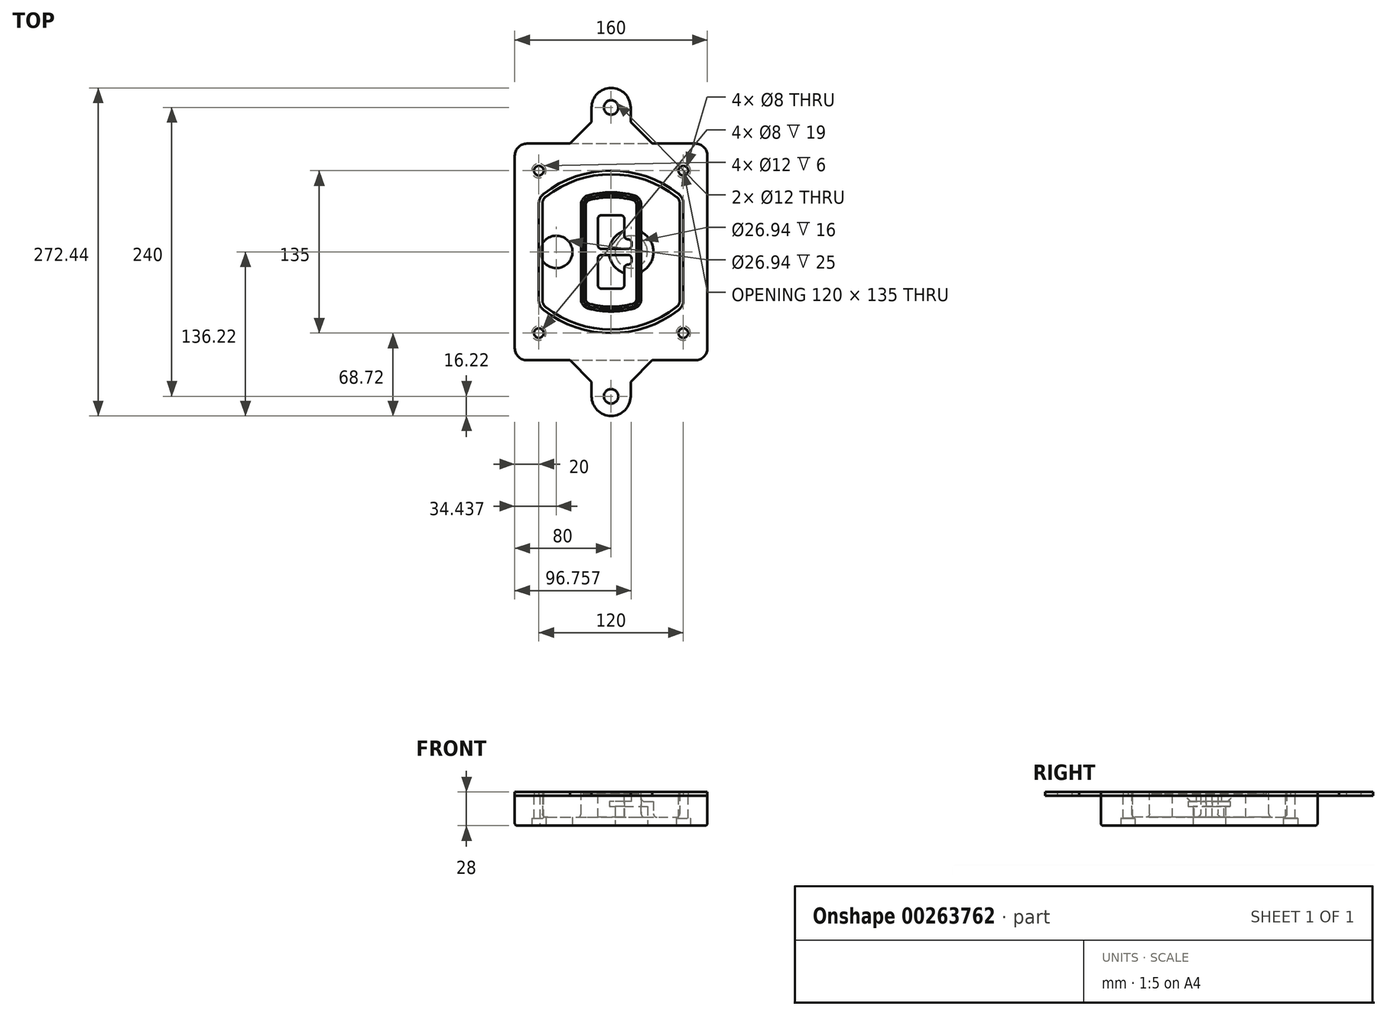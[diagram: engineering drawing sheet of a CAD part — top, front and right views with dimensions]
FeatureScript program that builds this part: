
annotation { "Feature Type Name" : "Feature", "Feature Type Description" : "" }
export const myFeature = defineFeature(function(context is Context, id is Id, definition is map)
    precondition{}
    {
        {
            var Q0;
            Q0=qCreatedBy(makeId("Top.planeOp"),FACE);
            var sketch = newSketch(context, id + "F0", { "sketchPlane" : qUnion([Q0])});
            skPoint(sketch, "E0.rect.middle", {"position": v(0, 0) * mm});
            skLineSegment(sketch, "E1.bottom", {"start": v(-70, -90) * mm, "end": v(70, -90) * mm});
            skLineSegment(sketch, "E1.top", {"start": v(-70, 90) * mm, "end": v(70, 90) * mm});
            skLineSegment(sketch, "E1.left", {"start": v(-80, -80) * mm, "end": v(-80, 80) * mm});
            skLineSegment(sketch, "E1.right", {"start": v(80, -80) * mm, "end": v(80, 80) * mm});
            skLineSegment(sketch, "E2", {"start": v(-80, 90) * mm, "end": v(80, -90) * mm, "construction": true});
            skLineSegment(sketch, "E3", {"start": v(80, 90) * mm, "end": v(-80, -90) * mm, "construction": true});
            skCircle(sketch, "E4", {"center": v(-60, 67.5) * mm, "radius": 4 * mm});
            skCircle(sketch, "E5", {"center": v(60, 67.5) * mm, "radius": 4 * mm});
            skCircle(sketch, "E6", {"center": v(60, -67.5) * mm, "radius": 4 * mm});
            skCircle(sketch, "E7", {"center": v(-60, -67.5) * mm, "radius": 4 * mm});
            skLineSegment(sketch, "E8", {"start": v(-60, 67.5) * mm, "end": v(60, 67.5) * mm, "construction": true});
            skLineSegment(sketch, "E9", {"start": v(60, 67.5) * mm, "end": v(60, -67.5) * mm, "construction": true});
            skLineSegment(sketch, "E10", {"start": v(60, -67.5) * mm, "end": v(-60, -67.5) * mm, "construction": true});
            skLineSegment(sketch, "E11", {"start": v(-60, -67.5) * mm, "end": v(-60, 67.5) * mm, "construction": true});
            skLineSegment(sketch, "E12", {"start": v(-60, 40.3) * mm, "end": v(-60, -40.3) * mm});
            skLineSegment(sketch, "E13", {"start": v(60, 40.3) * mm, "end": v(60, -40.3) * mm});
            skArc(sketch, "E14", {"start": v(56.15, 48.18) * mm, "mid": v(0, 67.5) * mm, "end": v(-56.15, 48.18) * mm});
            skArc(sketch, "E15", {"start": v(-56.15, -48.18) * mm, "mid": v(0, -67.5) * mm, "end": v(56.15, -48.18) * mm});
            skLineSegment(sketch, "E16", {"start": v(-60, 0) * mm, "end": v(60, 0) * mm, "construction": true});
            skPoint(sketch, "E17.visualSharp", {"position": v(-60, -45) * mm});
            skArc(sketch, "E17.filletArc", {"start": v(-60, -40.3) * mm, "mid": v(-58.99, -44.68) * mm, "end": v(-56.15, -48.18) * mm});
            skPoint(sketch, "E18.visualSharp", {"position": v(-60, 45) * mm});
            skArc(sketch, "E18.filletArc", {"start": v(-56.15, 48.18) * mm, "mid": v(-58.99, 44.68) * mm, "end": v(-60, 40.3) * mm});
            skPoint(sketch, "E19.visualSharp", {"position": v(60, 45) * mm});
            skArc(sketch, "E19.filletArc", {"start": v(60, 40.3) * mm, "mid": v(58.99, 44.68) * mm, "end": v(56.15, 48.18) * mm});
            skPoint(sketch, "E20.visualSharp", {"position": v(60, -45) * mm});
            skArc(sketch, "E20.filletArc", {"start": v(56.15, -48.18) * mm, "mid": v(58.99, -44.68) * mm, "end": v(60, -40.3) * mm});
            skPoint(sketch, "E21.visualSharp", {"position": v(-80, 90) * mm});
            skArc(sketch, "E21.filletArc", {"start": v(-70, 90) * mm, "mid": v(-77.07, 87.07) * mm, "end": v(-80, 80) * mm});
            skPoint(sketch, "E22.visualSharp", {"position": v(80, 90) * mm});
            skArc(sketch, "E22.filletArc", {"start": v(80, 80) * mm, "mid": v(77.07, 87.07) * mm, "end": v(70, 90) * mm});
            skPoint(sketch, "E23.visualSharp", {"position": v(80, -90) * mm});
            skArc(sketch, "E23.filletArc", {"start": v(70, -90) * mm, "mid": v(77.07, -87.07) * mm, "end": v(80, -80) * mm});
            skPoint(sketch, "E24.visualSharp", {"position": v(-80, -90) * mm});
            skArc(sketch, "E24.filletArc", {"start": v(-80, -80) * mm, "mid": v(-77.07, -87.07) * mm, "end": v(-70, -90) * mm});
            skArc(sketch, "E25.0", {"start": v(57, 40.3) * mm, "mid": v(56.3, 43.36) * mm, "end": v(54.3, 45.81) * mm});
            skLineSegment(sketch, "E25.1", {"start": v(57, 40.3) * mm, "end": v(57, -40.3) * mm});
            skArc(sketch, "E25.2", {"start": v(54.3, -45.81) * mm, "mid": v(56.3, -43.36) * mm, "end": v(57, -40.3) * mm});
            skArc(sketch, "E25.3", {"start": v(-54.3, -45.81) * mm, "mid": v(0, -64.5) * mm, "end": v(54.3, -45.81) * mm});
            skArc(sketch, "E25.4", {"start": v(-57, -40.3) * mm, "mid": v(-56.3, -43.36) * mm, "end": v(-54.3, -45.81) * mm});
            skArc(sketch, "E25.5", {"start": v(54.3, 45.81) * mm, "mid": v(0, 64.5) * mm, "end": v(-54.3, 45.81) * mm});
            skLineSegment(sketch, "E25.6", {"start": v(-57, 40.3) * mm, "end": v(-57, -40.3) * mm});
            skArc(sketch, "E25.7", {"start": v(-54.3, 45.81) * mm, "mid": v(-56.3, 43.36) * mm, "end": v(-57, 40.3) * mm});
            skArc(sketch, "E26.0", {"start": v(-58.62, 51.33) * mm, "mid": v(-62.58, 46.43) * mm, "end": v(-64, 40.3) * mm});
            skArc(sketch, "E26.1", {"start": v(58.62, 51.33) * mm, "mid": v(0, 71.5) * mm, "end": v(-58.62, 51.33) * mm});
            skArc(sketch, "E26.2", {"start": v(64, 40.3) * mm, "mid": v(62.58, 46.43) * mm, "end": v(58.62, 51.33) * mm});
            skLineSegment(sketch, "E26.3", {"start": v(64, 40.3) * mm, "end": v(64, -40.3) * mm});
            skArc(sketch, "E26.4", {"start": v(58.62, -51.33) * mm, "mid": v(62.58, -46.43) * mm, "end": v(64, -40.3) * mm});
            skLineSegment(sketch, "E26.5", {"start": v(-64, 40.3) * mm, "end": v(-64, -40.3) * mm});
            skArc(sketch, "E26.6", {"start": v(-58.62, -51.33) * mm, "mid": v(0, -71.5) * mm, "end": v(58.62, -51.33) * mm});
            skArc(sketch, "E26.7", {"start": v(-64, -40.3) * mm, "mid": v(-62.58, -46.43) * mm, "end": v(-58.62, -51.33) * mm});
            skSolve(sketch);
        }
        {
            var Q0;
            Q0=makeQuery(id+"F0.imprint","IMPRINT",FACE,{"disambiguationData":[TD([[makeQuery(id+"F0.imprint","IMPRINT",EDGE,{"derivedFrom":sQuery(id+"F0.wireOp",EDGE,"E1.bottom")}),1.0]])]});
            var Q1;
            Q1=makeQuery(id+"F0.imprint","IMPRINT",FACE,{"disambiguationData":[TD([[makeQuery(id+"F0.imprint","IMPRINT",EDGE,{"derivedFrom":sQuery(id+"F0.wireOp",EDGE,"E12")}),1.0]])]});
            var Q2;
            Q2=makeQuery(id+"F0.imprint","IMPRINT",FACE,{"disambiguationData":[TD([[makeQuery(id+"F0.imprint","IMPRINT",EDGE,{"derivedFrom":sQuery(id+"F0.wireOp",EDGE,"E25.0")}),1.0]])]});
            var Q3;
            Q3=makeQuery(id+"F0.imprint","IMPRINT",FACE,{"disambiguationData":[TD([[makeQuery(id+"F0.imprint","IMPRINT",EDGE,{"derivedFrom":sQuery(id+"F0.wireOp",EDGE,"E12")}),-1.0]])]});
            extrude(context, id + "F1", {"entities" : qUnion([Q0, Q1, Q2, Q3]), "oppositeDirection" : true, "depth" : 25 * mm});
        }
        {
            var Q0;
            Q0=makeQuery(id+"F0.imprint","IMPRINT",FACE,{"disambiguationData":[TD([[makeQuery(id+"F0.imprint","IMPRINT",EDGE,{"derivedFrom":sQuery(id+"F0.wireOp",EDGE,"E12")}),1.0]])]});
            extrude(context, id + "F2", {"entities" : qUnion([Q0]), "operationType" : NewBodyOperationType.ADD, "depth" : 3 * mm});
        }
        {
            var Q0;
            Q0=makeQuery(id+"F0.imprint","IMPRINT",FACE,{"disambiguationData":[TD([[makeQuery(id+"F0.imprint","IMPRINT",EDGE,{"derivedFrom":sQuery(id+"F0.wireOp",EDGE,"E25.0")}),1.0]])]});
            extrude(context, id + "F3", {"entities" : qUnion([Q0]), "operationType" : NewBodyOperationType.REMOVE, "oppositeDirection" : true, "depth" : 18 * mm});
        }
        {
            var Q0;
            Q0=makeQuery(id+"F2.opExtrude","CAP_FACE",FACE,{"disambiguationData":[OSD([sQuery(id+"F0.wireOp",EDGE,"E12"),sQuery(id+"F0.wireOp",EDGE,"E13"),sQuery(id+"F0.wireOp",EDGE,"E14"),sQuery(id+"F0.wireOp",EDGE,"E15"),sQuery(id+"F0.wireOp",EDGE,"E17.filletArc"),sQuery(id+"F0.wireOp",EDGE,"E18.filletArc"),sQuery(id+"F0.wireOp",EDGE,"E19.filletArc"),sQuery(id+"F0.wireOp",EDGE,"E20.filletArc"),sQuery(id+"F0.wireOp",EDGE,"E25.0"),sQuery(id+"F0.wireOp",EDGE,"E25.1"),sQuery(id+"F0.wireOp",EDGE,"E25.2"),sQuery(id+"F0.wireOp",EDGE,"E25.3"),sQuery(id+"F0.wireOp",EDGE,"E25.4"),sQuery(id+"F0.wireOp",EDGE,"E25.5"),sQuery(id+"F0.wireOp",EDGE,"E25.6"),sQuery(id+"F0.wireOp",EDGE,"E25.7")])],"isStart":false});
            var sketch = newSketch(context, id + "F4", { "sketchPlane" : qUnion([Q0])});
            skArc(sketch, "E27.0", {"start": v(-19.08, -46.97) * mm, "mid": v(0, -49.5) * mm, "end": v(19.08, -46.97) * mm});
            skArc(sketch, "E28.0", {"start": v(19.08, 46.97) * mm, "mid": v(0, 49.5) * mm, "end": v(-19.08, 46.97) * mm});
            skLineSegment(sketch, "E29", {"start": v(-25, 39.25) * mm, "end": v(-25, -39.25) * mm});
            skLineSegment(sketch, "E30", {"start": v(25, 39.25) * mm, "end": v(25, -39.25) * mm});
            skLineSegment(sketch, "E31", {"start": v(-25, 45.1) * mm, "end": v(25, 45.1) * mm, "construction": true});
            skLineSegment(sketch, "E32", {"start": v(-25, -45.1) * mm, "end": v(25, -45.1) * mm, "construction": true});
            skPoint(sketch, "E33.visualSharp", {"position": v(-25, 45.1) * mm});
            skArc(sketch, "E33.filletArc", {"start": v(-19.08, 46.97) * mm, "mid": v(-23.35, 44.11) * mm, "end": v(-25, 39.25) * mm});
            skPoint(sketch, "E34.visualSharp", {"position": v(25, 45.1) * mm});
            skArc(sketch, "E34.filletArc", {"start": v(25, 39.25) * mm, "mid": v(23.35, 44.11) * mm, "end": v(19.08, 46.97) * mm});
            skPoint(sketch, "E35.visualSharp", {"position": v(25, -45.1) * mm});
            skArc(sketch, "E35.filletArc", {"start": v(19.08, -46.97) * mm, "mid": v(23.35, -44.11) * mm, "end": v(25, -39.25) * mm});
            skPoint(sketch, "E36.visualSharp", {"position": v(-25, -45.1) * mm});
            skArc(sketch, "E36.filletArc", {"start": v(-25, -39.25) * mm, "mid": v(-23.35, -44.11) * mm, "end": v(-19.08, -46.97) * mm});
            skArc(sketch, "E37.0", {"start": v(54.3, 45.81) * mm, "mid": v(0, 64.5) * mm, "end": v(-54.3, 45.81) * mm});
            skArc(sketch, "E37.1", {"start": v(-54.3, 45.81) * mm, "mid": v(-56.3, 43.36) * mm, "end": v(-57, 40.3) * mm});
            skLineSegment(sketch, "E37.2", {"start": v(-57, 40.3) * mm, "end": v(-57, -40.3) * mm});
            skArc(sketch, "E37.3", {"start": v(-57, -40.3) * mm, "mid": v(-56.3, -43.36) * mm, "end": v(-54.3, -45.81) * mm});
            skArc(sketch, "E37.4", {"start": v(-54.3, -45.81) * mm, "mid": v(0, -64.5) * mm, "end": v(54.3, -45.81) * mm});
            skArc(sketch, "E37.5", {"start": v(54.3, -45.81) * mm, "mid": v(56.3, -43.36) * mm, "end": v(57, -40.3) * mm});
            skLineSegment(sketch, "E37.6", {"start": v(57, 40.3) * mm, "end": v(57, -40.3) * mm});
            skArc(sketch, "E37.7", {"start": v(57, 40.3) * mm, "mid": v(56.3, 43.36) * mm, "end": v(54.3, 45.81) * mm});
            skLineSegment(sketch, "E38.0", {"start": v(23, 39.25) * mm, "end": v(23, -39.25) * mm});
            skArc(sketch, "E38.1", {"start": v(18.56, -45.04) * mm, "mid": v(21.76, -42.9) * mm, "end": v(23, -39.25) * mm});
            skArc(sketch, "E38.2", {"start": v(-18.56, -45.04) * mm, "mid": v(0, -47.5) * mm, "end": v(18.56, -45.04) * mm});
            skArc(sketch, "E38.3", {"start": v(-23, -39.25) * mm, "mid": v(-21.76, -42.9) * mm, "end": v(-18.56, -45.04) * mm});
            skLineSegment(sketch, "E38.4", {"start": v(-23, 39.25) * mm, "end": v(-23, -39.25) * mm});
            skArc(sketch, "E38.5", {"start": v(23, 39.25) * mm, "mid": v(21.76, 42.9) * mm, "end": v(18.56, 45.04) * mm});
            skArc(sketch, "E38.6", {"start": v(-18.56, 45.04) * mm, "mid": v(-21.76, 42.9) * mm, "end": v(-23, 39.25) * mm});
            skArc(sketch, "E38.7", {"start": v(18.56, 45.04) * mm, "mid": v(0, 47.5) * mm, "end": v(-18.56, 45.04) * mm});
            skArc(sketch, "E39.0", {"start": v(21, 39.25) * mm, "mid": v(20.18, 41.68) * mm, "end": v(18.04, 43.1) * mm});
            skLineSegment(sketch, "E39.1", {"start": v(21, 39.25) * mm, "end": v(21, -39.25) * mm});
            skArc(sketch, "E39.2", {"start": v(18.04, -43.1) * mm, "mid": v(20.18, -41.68) * mm, "end": v(21, -39.25) * mm});
            skArc(sketch, "E39.3", {"start": v(-18.04, -43.1) * mm, "mid": v(0, -45.5) * mm, "end": v(18.04, -43.1) * mm});
            skArc(sketch, "E39.4", {"start": v(-21, -39.25) * mm, "mid": v(-20.18, -41.68) * mm, "end": v(-18.04, -43.1) * mm});
            skArc(sketch, "E39.5", {"start": v(18.04, 43.1) * mm, "mid": v(0, 45.5) * mm, "end": v(-18.04, 43.1) * mm});
            skLineSegment(sketch, "E39.6", {"start": v(-21, 39.25) * mm, "end": v(-21, -39.25) * mm});
            skArc(sketch, "E39.7", {"start": v(-18.04, 43.1) * mm, "mid": v(-20.18, 41.68) * mm, "end": v(-21, 39.25) * mm});
            skLineSegment(sketch, "E40", {"start": v(-25, 0) * mm, "end": v(25, 0) * mm, "construction": true});
            skLineSegment(sketch, "E41", {"start": v(-11, 5.5) * mm, "end": v(-11, 27.5) * mm});
            skLineSegment(sketch, "E42", {"start": v(-8, 30.5) * mm, "end": v(8, 30.5) * mm});
            skLineSegment(sketch, "E43", {"start": v(11, 27.5) * mm, "end": v(11, 13.5) * mm});
            skLineSegment(sketch, "E44", {"start": v(14, 10.5) * mm, "end": v(14, 10.5) * mm});
            skLineSegment(sketch, "E45", {"start": v(17, 7.5) * mm, "end": v(17, 5.5) * mm});
            skLineSegment(sketch, "E46", {"start": v(14, 2.5) * mm, "end": v(-8, 2.5) * mm});
            skPoint(sketch, "E47.visualSharp", {"position": v(-11, 30.5) * mm});
            skArc(sketch, "E47.filletArc", {"start": v(-8, 30.5) * mm, "mid": v(-10.12, 29.62) * mm, "end": v(-11, 27.5) * mm});
            skPoint(sketch, "E48.visualSharp", {"position": v(11, 30.5) * mm});
            skArc(sketch, "E48.filletArc", {"start": v(11, 27.5) * mm, "mid": v(10.12, 29.62) * mm, "end": v(8, 30.5) * mm});
            skPoint(sketch, "E49.visualSharp", {"position": v(11, 10.5) * mm});
            skArc(sketch, "E49.filletArc", {"start": v(11, 13.5) * mm, "mid": v(11.88, 11.38) * mm, "end": v(14, 10.5) * mm});
            skPoint(sketch, "E50.visualSharp", {"position": v(17, 10.5) * mm});
            skArc(sketch, "E50.filletArc", {"start": v(17, 7.5) * mm, "mid": v(16.12, 9.62) * mm, "end": v(14, 10.5) * mm});
            skPoint(sketch, "E51.visualSharp", {"position": v(17, 2.5) * mm});
            skArc(sketch, "E51.filletArc", {"start": v(14, 2.5) * mm, "mid": v(16.12, 3.38) * mm, "end": v(17, 5.5) * mm});
            skPoint(sketch, "E52.visualSharp", {"position": v(-11, 2.5) * mm});
            skArc(sketch, "E52.filletArc", {"start": v(-11, 5.5) * mm, "mid": v(-10.12, 3.38) * mm, "end": v(-8, 2.5) * mm});
            skLineSegment(sketch, "E53.0.MirrorCS", {"start": v(14, -2.5) * mm, "end": v(-8, -2.5) * mm});
            skArc(sketch, "E54.0.MirrorCS", {"start": v(-11, -5.5) * mm, "mid": v(-10.12, -3.38) * mm, "end": v(-8, -2.5) * mm});
            skLineSegment(sketch, "E55.0.MirrorCS", {"start": v(-11, -5.5) * mm, "end": v(-11, -27.5) * mm});
            skArc(sketch, "E56.0.MirrorCS", {"start": v(-8, -30.5) * mm, "mid": v(-10.12, -29.62) * mm, "end": v(-11, -27.5) * mm});
            skLineSegment(sketch, "E57.0.MirrorCS", {"start": v(-8, -30.5) * mm, "end": v(8, -30.5) * mm});
            skArc(sketch, "E58.0.MirrorCS", {"start": v(11, -27.5) * mm, "mid": v(10.12, -29.62) * mm, "end": v(8, -30.5) * mm});
            skLineSegment(sketch, "E59.0.MirrorCS", {"start": v(11, -27.5) * mm, "end": v(11, -13.5) * mm});
            skArc(sketch, "E60.0.MirrorCS", {"start": v(11, -13.5) * mm, "mid": v(11.88, -11.38) * mm, "end": v(14, -10.5) * mm});
            skArc(sketch, "E61.0.MirrorCS", {"start": v(17, -7.5) * mm, "mid": v(16.12, -9.62) * mm, "end": v(14, -10.5) * mm});
            skLineSegment(sketch, "E62.0.MirrorCS", {"start": v(17, -7.5) * mm, "end": v(17, -5.5) * mm});
            skArc(sketch, "E63.0.MirrorCS", {"start": v(14, -2.5) * mm, "mid": v(16.12, -3.38) * mm, "end": v(17, -5.5) * mm});
            skSolve(sketch);
        }
        {
            var Q0;
            Q0=makeQuery(id+"F4.imprint","IMPRINT",FACE,{"disambiguationData":[TD([[makeQuery(id+"F4.imprint","IMPRINT",EDGE,{"derivedFrom":sQuery(id+"F4.wireOp",EDGE,"E27.0")}),1.0]])]});
            var Q1;
            Q1=makeQuery(id+"F4.imprint","IMPRINT",FACE,{"disambiguationData":[TD([[makeQuery(id+"F4.imprint","IMPRINT",EDGE,{"derivedFrom":sQuery(id+"F4.wireOp",EDGE,"E38.0")}),-1.0]])]});
            var Q2;
            Q2=makeQuery(id+"F4.imprint","IMPRINT",FACE,{"disambiguationData":[TD([[makeQuery(id+"F4.imprint","IMPRINT",EDGE,{"derivedFrom":sQuery(id+"F4.wireOp",EDGE,"E39.0")}),1.0]])]});
            extrude(context, id + "F5", {"entities" : qUnion([Q0, Q1, Q2]), "operationType" : NewBodyOperationType.ADD, "endBound" : BoundingType.UP_TO_NEXT, "oppositeDirection" : true, "depth" : 25 * mm});
        }
        {
            var Q0;
            Q0=makeQuery(id+"F4.imprint","IMPRINT",FACE,{"disambiguationData":[TD([[makeQuery(id+"F4.imprint","IMPRINT",EDGE,{"derivedFrom":sQuery(id+"F4.wireOp",EDGE,"E38.0")}),-1.0]])]});
            extrude(context, id + "F6", {"entities" : qUnion([Q0]), "operationType" : NewBodyOperationType.REMOVE, "oppositeDirection" : true, "depth" : 2 * mm});
        }
        {
            var Q0;
            Q0=makeQuery(id+"F1.opExtrude","CAP_FACE",FACE,{"disambiguationData":[OSD([sQuery(id+"F0.wireOp",EDGE,"E1.bottom"),sQuery(id+"F0.wireOp",EDGE,"E1.top"),sQuery(id+"F0.wireOp",EDGE,"E1.left"),sQuery(id+"F0.wireOp",EDGE,"E1.right"),sQuery(id+"F0.wireOp",EDGE,"E4"),sQuery(id+"F0.wireOp",EDGE,"E5"),sQuery(id+"F0.wireOp",EDGE,"E6"),sQuery(id+"F0.wireOp",EDGE,"E7"),sQuery(id+"F0.wireOp",EDGE,"E21.filletArc"),sQuery(id+"F0.wireOp",EDGE,"E22.filletArc"),sQuery(id+"F0.wireOp",EDGE,"E23.filletArc"),sQuery(id+"F0.wireOp",EDGE,"E24.filletArc")])],"isStart":false});
            var sketch = newSketch(context, id + "F7", { "sketchPlane" : qUnion([Q0])});
            skCircle(sketch, "E64", {"center": v(16.76, 0) * mm, "radius": 13.47 * mm});
            skCircle(sketch, "E65", {"center": v(-45.56, 0) * mm, "radius": 13.47 * mm});
            skLineSegment(sketch, "E66", {"start": v(80, 0) * mm, "end": v(-80, 0) * mm});
            skCircle(sketch, "E67", {"center": v(16.76, 0) * mm, "radius": 18.47 * mm});
            skCircle(sketch, "E68", {"center": v(60, -67.5) * mm, "radius": 6 * mm});
            skCircle(sketch, "E69", {"center": v(-60, -67.5) * mm, "radius": 6 * mm});
            skCircle(sketch, "E70", {"center": v(-60, 67.5) * mm, "radius": 6 * mm});
            skCircle(sketch, "E71", {"center": v(60, 67.5) * mm, "radius": 6 * mm});
            skSolve(sketch);
        }
        {
            var Q0;
            {var subQ1=sQuery(id+"F7.wireOp",EDGE,"E66");var subQ4=sQuery(id+"F7.wireOp",EDGE,"E64");var subQ6=makeQuery(id+"F7.imprint","INTERSECT",VERTEX,{"disambiguationData":[OD(0.0)],"derivedFrom":[subQ4,subQ1]});Q0=makeQuery(id+"F7.imprint","IMPRINT",FACE,{"disambiguationData":[TD([[makeQuery(id+"F7.imprint","IMPRINT",EDGE,{"disambiguationData":[TD([[subQ6,-1.0]])],"derivedFrom":subQ4}),-1.0]])]});}
            var Q1;
            {var subQ0=sQuery(id+"F7.wireOp",EDGE,"E66");var subQ1=sQuery(id+"F7.wireOp",EDGE,"E64");var subQ3=makeQuery(id+"F7.imprint","INTERSECT",VERTEX,{"disambiguationData":[OD(0.0)],"derivedFrom":[subQ1,subQ0]});Q1=makeQuery(id+"F7.imprint","IMPRINT",FACE,{"disambiguationData":[TD([[makeQuery(id+"F7.imprint","IMPRINT",EDGE,{"disambiguationData":[TD([[subQ3,-1.0]])],"derivedFrom":subQ1}),1.0]])]});}
            var Q2;
            {var subQ0=sQuery(id+"F7.wireOp",EDGE,"E66");var subQ1=sQuery(id+"F7.wireOp",EDGE,"E64");var subQ3=makeQuery(id+"F7.imprint","INTERSECT",VERTEX,{"disambiguationData":[OD(0.0)],"derivedFrom":[subQ1,subQ0]});Q2=makeQuery(id+"F7.imprint","IMPRINT",FACE,{"disambiguationData":[TD([[makeQuery(id+"F7.imprint","IMPRINT",EDGE,{"disambiguationData":[TD([[subQ3,1.0]])],"derivedFrom":subQ1}),1.0]])]});}
            var Q3;
            {var subQ1=sQuery(id+"F7.wireOp",EDGE,"E66");var subQ4=sQuery(id+"F7.wireOp",EDGE,"E64");var subQ6=makeQuery(id+"F7.imprint","INTERSECT",VERTEX,{"disambiguationData":[OD(0.0)],"derivedFrom":[subQ4,subQ1]});Q3=makeQuery(id+"F7.imprint","IMPRINT",FACE,{"disambiguationData":[TD([[makeQuery(id+"F7.imprint","IMPRINT",EDGE,{"disambiguationData":[TD([[subQ6,1.0]])],"derivedFrom":subQ4}),-1.0]])]});}
            extrude(context, id + "F8", {"entities" : qUnion([Q0, Q1, Q2, Q3]), "operationType" : NewBodyOperationType.ADD, "oppositeDirection" : true, "depth" : 20 * mm});
        }
        {
            var Q0;
            {var subQ0=sQuery(id+"F7.wireOp",EDGE,"E66");var subQ1=sQuery(id+"F7.wireOp",EDGE,"E64");var subQ3=makeQuery(id+"F7.imprint","INTERSECT",VERTEX,{"disambiguationData":[OD(0.0)],"derivedFrom":[subQ1,subQ0]});Q0=makeQuery(id+"F7.imprint","IMPRINT",FACE,{"disambiguationData":[TD([[makeQuery(id+"F7.imprint","IMPRINT",EDGE,{"disambiguationData":[TD([[subQ3,-1.0]])],"derivedFrom":subQ1}),1.0]])]});}
            var Q1;
            {var subQ0=sQuery(id+"F7.wireOp",EDGE,"E66");var subQ1=sQuery(id+"F7.wireOp",EDGE,"E64");var subQ3=makeQuery(id+"F7.imprint","INTERSECT",VERTEX,{"disambiguationData":[OD(0.0)],"derivedFrom":[subQ1,subQ0]});Q1=makeQuery(id+"F7.imprint","IMPRINT",FACE,{"disambiguationData":[TD([[makeQuery(id+"F7.imprint","IMPRINT",EDGE,{"disambiguationData":[TD([[subQ3,1.0]])],"derivedFrom":subQ1}),1.0]])]});}
            extrude(context, id + "F9", {"entities" : qUnion([Q0, Q1]), "operationType" : NewBodyOperationType.REMOVE, "oppositeDirection" : true, "depth" : 16 * mm});
        }
        {
            var Q0;
            {var subQ0=sQuery(id+"F7.wireOp",EDGE,"E66");var subQ1=sQuery(id+"F7.wireOp",EDGE,"E65");var subQ3=makeQuery(id+"F7.imprint","INTERSECT",VERTEX,{"disambiguationData":[OD(0.0)],"derivedFrom":[subQ1,subQ0]});Q0=makeQuery(id+"F7.imprint","IMPRINT",FACE,{"disambiguationData":[TD([[makeQuery(id+"F7.imprint","IMPRINT",EDGE,{"disambiguationData":[TD([[subQ3,-1.0]])],"derivedFrom":subQ1}),1.0]])]});}
            var Q1;
            {var subQ0=sQuery(id+"F7.wireOp",EDGE,"E66");var subQ1=sQuery(id+"F7.wireOp",EDGE,"E65");var subQ3=makeQuery(id+"F7.imprint","INTERSECT",VERTEX,{"disambiguationData":[OD(0.0)],"derivedFrom":[subQ1,subQ0]});Q1=makeQuery(id+"F7.imprint","IMPRINT",FACE,{"disambiguationData":[TD([[makeQuery(id+"F7.imprint","IMPRINT",EDGE,{"disambiguationData":[TD([[subQ3,1.0]])],"derivedFrom":subQ1}),1.0]])]});}
            extrude(context, id + "F10", {"entities" : qUnion([Q0, Q1]), "operationType" : NewBodyOperationType.REMOVE, "oppositeDirection" : true, "depth" : 25 * mm});
        }
        {
            var Q0;
            Q0=makeQuery(id+"F7.imprint","IMPRINT",FACE,{"disambiguationData":[TD([[makeQuery(id+"F7.imprint","IMPRINT",EDGE,{"derivedFrom":sQuery(id+"F7.wireOp",EDGE,"E68")}),1.0]])]});
            var Q1;
            Q1=makeQuery(id+"F7.imprint","IMPRINT",FACE,{"disambiguationData":[TD([[makeQuery(id+"F7.imprint","IMPRINT",EDGE,{"derivedFrom":makeQuery(id+"F1.opExtrude","CAP_EDGE",EDGE,{"disambiguationData":[OSD([sQuery(id+"F0.wireOp",EDGE,"E5")])],"isStart":false})}),-1.0]])]});
            var Q2;
            Q2=makeQuery(id+"F7.imprint","IMPRINT",FACE,{"disambiguationData":[TD([[makeQuery(id+"F7.imprint","IMPRINT",EDGE,{"derivedFrom":sQuery(id+"F7.wireOp",EDGE,"E69")}),1.0]])]});
            var Q3;
            Q3=makeQuery(id+"F7.imprint","IMPRINT",FACE,{"disambiguationData":[TD([[makeQuery(id+"F7.imprint","IMPRINT",EDGE,{"derivedFrom":makeQuery(id+"F1.opExtrude","CAP_EDGE",EDGE,{"disambiguationData":[OSD([sQuery(id+"F0.wireOp",EDGE,"E4")])],"isStart":false})}),-1.0]])]});
            var Q4;
            Q4=makeQuery(id+"F7.imprint","IMPRINT",FACE,{"disambiguationData":[TD([[makeQuery(id+"F7.imprint","IMPRINT",EDGE,{"derivedFrom":sQuery(id+"F7.wireOp",EDGE,"E70")}),1.0]])]});
            var Q5;
            Q5=makeQuery(id+"F7.imprint","IMPRINT",FACE,{"disambiguationData":[TD([[makeQuery(id+"F7.imprint","IMPRINT",EDGE,{"derivedFrom":makeQuery(id+"F1.opExtrude","CAP_EDGE",EDGE,{"disambiguationData":[OSD([sQuery(id+"F0.wireOp",EDGE,"E7")])],"isStart":false})}),-1.0]])]});
            var Q6;
            Q6=makeQuery(id+"F7.imprint","IMPRINT",FACE,{"disambiguationData":[TD([[makeQuery(id+"F7.imprint","IMPRINT",EDGE,{"derivedFrom":sQuery(id+"F7.wireOp",EDGE,"E71")}),1.0]])]});
            var Q7;
            Q7=makeQuery(id+"F7.imprint","IMPRINT",FACE,{"disambiguationData":[TD([[makeQuery(id+"F7.imprint","IMPRINT",EDGE,{"derivedFrom":makeQuery(id+"F1.opExtrude","CAP_EDGE",EDGE,{"disambiguationData":[OSD([sQuery(id+"F0.wireOp",EDGE,"E6")])],"isStart":false})}),-1.0]])]});
            extrude(context, id + "F11", {"entities" : qUnion([Q0, Q1, Q2, Q3, Q4, Q5, Q6, Q7]), "operationType" : NewBodyOperationType.REMOVE, "oppositeDirection" : true, "depth" : 6 * mm});
        }
        {
            var Q0;
            Q0=makeQuery(id+"F9.boolean.opBoolean","COPY",FACE,{"derivedFrom":makeQuery(id+"F9.opExtrude","CAP_FACE",FACE,{"disambiguationData":[OSD([sQuery(id+"F7.wireOp",EDGE,"E64")])],"isStart":false})});
            var sketch = newSketch(context, id + "F12", { "sketchPlane" : qUnion([Q0])});
            skArc(sketch, "E72.0", {"start": v(11, 17.55) * mm, "mid": v(2.57, 11.82) * mm, "end": v(-1.54, 2.5) * mm});
            skArc(sketch, "E72.1", {"start": v(-1.54, -2.5) * mm, "mid": v(2.57, -11.82) * mm, "end": v(11, -17.55) * mm});
            skLineSegment(sketch, "E73", {"start": v(-1.54, -2.5) * mm, "end": v(14, -2.5) * mm});
            skLineSegment(sketch, "E74.0", {"start": v(14, 2.5) * mm, "end": v(-1.54, 2.5) * mm});
            skArc(sketch, "E74.1", {"start": v(14, 2.5) * mm, "mid": v(16.12, 3.38) * mm, "end": v(17, 5.5) * mm});
            skLineSegment(sketch, "E74.2", {"start": v(17, 7.5) * mm, "end": v(17, 5.5) * mm});
            skArc(sketch, "E74.3", {"start": v(17, 7.5) * mm, "mid": v(16.12, 9.62) * mm, "end": v(14, 10.5) * mm});
            skArc(sketch, "E74.4", {"start": v(11, 13.5) * mm, "mid": v(11.88, 11.38) * mm, "end": v(14, 10.5) * mm});
            skLineSegment(sketch, "E74.5", {"start": v(11, 17.55) * mm, "end": v(11, 13.5) * mm});
            skLineSegment(sketch, "E74.7", {"start": v(14, -2.5) * mm, "end": v(-1.54, -2.5) * mm});
            skArc(sketch, "E74.8", {"start": v(14, -2.5) * mm, "mid": v(16.12, -3.38) * mm, "end": v(17, -5.5) * mm});
            skLineSegment(sketch, "E74.9", {"start": v(17, -7.5) * mm, "end": v(17, -5.5) * mm});
            skArc(sketch, "E74.10", {"start": v(17, -7.5) * mm, "mid": v(16.12, -9.62) * mm, "end": v(14, -10.5) * mm});
            skArc(sketch, "E74.11", {"start": v(11, -13.5) * mm, "mid": v(11.88, -11.38) * mm, "end": v(14, -10.5) * mm});
            skLineSegment(sketch, "E74.12", {"start": v(11, -17.55) * mm, "end": v(11, -13.5) * mm});
            skPoint(sketch, "E75.orphan", {"position": v(11, -27.5) * mm});
            skPoint(sketch, "E76.orphan", {"position": v(-8, -2.5) * mm});
            skPoint(sketch, "E77.orphan", {"position": v(-8, 2.5) * mm});
            skPoint(sketch, "E78.orphan", {"position": v(11, 27.5) * mm});
            skSolve(sketch);
        }
        {
            var Q0;
            {var subQ7=sQuery(id+"F12.wireOp",EDGE,"E72.0");var subQ14=sQuery(id+"F12.wireOp",EDGE,"E72.1");var subQ16=sQuery(id+"F12.wireOp",EDGE,"E74.1");var subQ18=sQuery(id+"F12.wireOp",EDGE,"E74.8");Q0=qUnion([makeQuery(id+"F12.imprint","IMPRINT",FACE,{"disambiguationData":[TD([[makeQuery(id+"F12.imprint","IMPRINT",EDGE,{"derivedFrom":subQ7}),1.0]])]}),makeQuery(id+"F12.imprint","IMPRINT",FACE,{"disambiguationData":[TD([[makeQuery(id+"F12.imprint","IMPRINT",EDGE,{"derivedFrom":subQ14}),1.0]])]}),makeQuery(id+"F12.imprint","IMPRINT",FACE,{"disambiguationData":[TD([[makeQuery(id+"F12.imprint","IMPRINT",EDGE,{"derivedFrom":subQ16}),1.0]])]}),makeQuery(id+"F12.imprint","IMPRINT",FACE,{"disambiguationData":[TD([[makeQuery(id+"F12.imprint","IMPRINT",EDGE,{"derivedFrom":subQ18}),-1.0]])]})]);}
            var Q1;
            Q1=makeQuery(id+"F5.boolean.opBoolean","SPLIT",FACE,{"disambiguationData":[TD([makeQuery(id+"F5.opExtrude","SWEPT_FACE",FACE,{"disambiguationData":[OSD([sQuery(id+"F4.wireOp",EDGE,"E41")])]})])],"derivedFrom":makeQuery(id+"F3.boolean.opBoolean","COPY",FACE,{"derivedFrom":makeQuery(id+"F3.opExtrude","CAP_FACE",FACE,{"disambiguationData":[OSD([sQuery(id+"F0.wireOp",EDGE,"E25.0"),sQuery(id+"F0.wireOp",EDGE,"E25.1"),sQuery(id+"F0.wireOp",EDGE,"E25.2"),sQuery(id+"F0.wireOp",EDGE,"E25.3"),sQuery(id+"F0.wireOp",EDGE,"E25.4"),sQuery(id+"F0.wireOp",EDGE,"E25.5"),sQuery(id+"F0.wireOp",EDGE,"E25.6"),sQuery(id+"F0.wireOp",EDGE,"E25.7")])],"isStart":false})})});
            extrude(context, id + "F13", {"entities" : qUnion([Q0]), "operationType" : NewBodyOperationType.REMOVE, "endBound" : BoundingType.UP_TO_SURFACE, "endBoundEntityFace" : qUnion([Q1]), "depth" : 25 * mm});
        }
        {
            var Q0;
            Q0=makeQuery(id+"F3.boolean.opBoolean","COPY",EDGE,{"derivedFrom":makeQuery(id+"F3.opExtrude","CAP_EDGE",EDGE,{"disambiguationData":[OSD([sQuery(id+"F0.wireOp",EDGE,"E25.6")])],"isStart":false})});
            var Q1;
            Q1=makeQuery(id+"F8.boolean.opBoolean","INTERSECT",EDGE,{"derivedFrom":[makeQuery(id+"F5.opExtrude","SWEPT_FACE",FACE,{"disambiguationData":[OSD([sQuery(id+"F4.wireOp",EDGE,"E30")])]}),makeQuery(id+"F8.opExtrude","CAP_FACE",FACE,{"disambiguationData":[OSD([sQuery(id+"F7.wireOp",EDGE,"E67")])],"isStart":false})]});
            var Q2;
            Q2=makeQuery(id+"F8.boolean.opBoolean","INTERSECT",EDGE,{"disambiguationData":[OD(1.0)],"derivedFrom":[makeQuery(id+"F5.opExtrude","SWEPT_FACE",FACE,{"disambiguationData":[OSD([sQuery(id+"F4.wireOp",EDGE,"E30")])]}),makeQuery(id+"F8.opExtrude","SWEPT_FACE",FACE,{"disambiguationData":[OSD([sQuery(id+"F7.wireOp",EDGE,"E67")])]})]});
            var Q3;
            {var subQ0=sQuery(id+"F4.wireOp",EDGE,"E30");Q3=makeQuery(id+"F8.boolean.opBoolean","SPLIT",EDGE,{"disambiguationData":[TD([makeQuery(id+"F5.opExtrude","SWEPT_FACE",FACE,{"disambiguationData":[OSD([sQuery(id+"F4.wireOp",EDGE,"E35.filletArc")])]})])],"derivedFrom":makeQuery(id+"F5.opExtrude","CAP_EDGE",EDGE,{"disambiguationData":[OSD([subQ0])],"isStart":false})});}
            var Q4;
            {var subQ0=sQuery(id+"F0.wireOp",EDGE,"E25.7");var subQ1=sQuery(id+"F0.wireOp",EDGE,"E25.1");var subQ2=sQuery(id+"F0.wireOp",EDGE,"E25.6");var subQ3=sQuery(id+"F0.wireOp",EDGE,"E25.5");var subQ4=sQuery(id+"F0.wireOp",EDGE,"E25.4");var subQ5=sQuery(id+"F0.wireOp",EDGE,"E25.0");var subQ6=sQuery(id+"F0.wireOp",EDGE,"E25.2");var subQ7=sQuery(id+"F0.wireOp",EDGE,"E25.3");Q4=makeQuery(id+"F8.boolean.opBoolean","INTERSECT",EDGE,{"derivedFrom":[makeQuery(id+"F5.boolean.opBoolean","SPLIT",FACE,{"disambiguationData":[TD([makeQuery(id+"F2.opExtrude","SWEPT_FACE",FACE,{"disambiguationData":[OSD([subQ5])]})])],"derivedFrom":makeQuery(id+"F3.boolean.opBoolean","COPY",FACE,{"derivedFrom":makeQuery(id+"F3.opExtrude","CAP_FACE",FACE,{"disambiguationData":[OSD([subQ5,subQ1,subQ6,subQ7,subQ4,subQ3,subQ2,subQ0])],"isStart":false})})}),makeQuery(id+"F8.opExtrude","SWEPT_FACE",FACE,{"disambiguationData":[OSD([sQuery(id+"F7.wireOp",EDGE,"E67")])]})]});}
            var Q5;
            Q5=makeQuery(id+"F8.boolean.opBoolean","INTERSECT",EDGE,{"disambiguationData":[OD(0.0)],"derivedFrom":[makeQuery(id+"F5.opExtrude","SWEPT_FACE",FACE,{"disambiguationData":[OSD([sQuery(id+"F4.wireOp",EDGE,"E30")])]}),makeQuery(id+"F8.opExtrude","SWEPT_FACE",FACE,{"disambiguationData":[OSD([sQuery(id+"F7.wireOp",EDGE,"E67")])]})]});
            fillet(context, id + "F14", {"entities" : qUnion([Q0, Q1, Q2, Q3, Q4, Q5]), "radius" : 3 * mm, "tangentPropagation" : true, "allowEdgeOverflow" : false});
        }
        {
            var Q0;
            Q0=makeQuery(id+"F1.opExtrude","CAP_EDGE",EDGE,{"disambiguationData":[OSD([sQuery(id+"F0.wireOp",EDGE,"E1.bottom")])],"isStart":false});
            fillet(context, id + "F15", {"entities" : qUnion([Q0]), "radius" : 2 * mm, "tangentPropagation" : true, "allowEdgeOverflow" : false});
        }
        {
            var Q0;
            {var subQ0=sQuery(id+"F0.wireOp",EDGE,"E22.filletArc");var subQ1=sQuery(id+"F0.wireOp",EDGE,"E7");var subQ2=sQuery(id+"F0.wireOp",EDGE,"E6");var subQ3=sQuery(id+"F0.wireOp",EDGE,"E5");var subQ4=sQuery(id+"F0.wireOp",EDGE,"E4");var subQ5=sQuery(id+"F0.wireOp",EDGE,"E1.bottom");var subQ6=sQuery(id+"F0.wireOp",EDGE,"E21.filletArc");var subQ7=sQuery(id+"F0.wireOp",EDGE,"E1.top");var subQ8=sQuery(id+"F0.wireOp",EDGE,"E1.left");var subQ9=sQuery(id+"F0.wireOp",EDGE,"E1.right");var subQ10=sQuery(id+"F0.wireOp",EDGE,"E23.filletArc");var subQ11=sQuery(id+"F0.wireOp",EDGE,"E24.filletArc");Q0=makeQuery(id+"F2.boolean.opBoolean","SPLIT",FACE,{"disambiguationData":[TD([makeQuery(id+"F1.opExtrude","SWEPT_FACE",FACE,{"disambiguationData":[OSD([subQ5])]})])],"derivedFrom":makeQuery(id+"F1.opExtrude","CAP_FACE",FACE,{"disambiguationData":[OSD([subQ5,subQ7,subQ8,subQ9,subQ4,subQ3,subQ2,subQ1,subQ6,subQ0,subQ10,subQ11])],"isStart":true})});}
            var sketch = newSketch(context, id + "F16", { "sketchPlane" : qUnion([Q0])});
            skLineSegment(sketch, "E79", {"start": v(0, 90) * mm, "end": v(0, 120) * mm, "construction": true});
            skCircle(sketch, "E80", {"center": v(0, 120) * mm, "radius": 6 * mm});
            skLineSegment(sketch, "E81", {"start": v(-16.22, 120) * mm, "end": v(-16.22, 108) * mm});
            skLineSegment(sketch, "E82", {"start": v(16.22, 120) * mm, "end": v(16.22, 108) * mm});
            skArc(sketch, "E83", {"start": v(-16.22, 120) * mm, "mid": v(0, 136.22) * mm, "end": v(16.22, 120) * mm});
            skLineSegment(sketch, "E84", {"start": v(-16.22, 108) * mm, "end": v(-34.22, 90) * mm});
            skLineSegment(sketch, "E85", {"start": v(16.22, 108) * mm, "end": v(34.22, 90) * mm});
            skLineSegment(sketch, "E86", {"start": v(-80, 0) * mm, "end": v(80, 0) * mm, "construction": true});
            skLineSegment(sketch, "E87.MirrorCS", {"start": v(-16.22, -108) * mm, "end": v(-34.22, -90) * mm});
            skLineSegment(sketch, "E88.MirrorCS", {"start": v(-16.22, -120) * mm, "end": v(-16.22, -108) * mm});
            skArc(sketch, "E89.MirrorCS", {"start": v(-16.22, -120) * mm, "mid": v(0, -136.22) * mm, "end": v(16.22, -120) * mm});
            skLineSegment(sketch, "E90.MirrorCS", {"start": v(16.22, -120) * mm, "end": v(16.22, -108) * mm});
            skLineSegment(sketch, "E91.MirrorCS", {"start": v(16.22, -108) * mm, "end": v(34.22, -90) * mm});
            skCircle(sketch, "E92.MirrorC", {"center": v(0, -120) * mm, "radius": 6 * mm});
            skLineSegment(sketch, "E93.MirrorCS", {"start": v(0, -90) * mm, "end": v(0, -120) * mm, "construction": true});
            skSolve(sketch);
        }
        {
            var Q0;
            {var subQ0=sQuery(id+"F16.wireOp",EDGE,"E87.MirrorCS");Q0=makeQuery(id+"F16.imprint","IMPRINT",FACE,{"disambiguationData":[TD([[makeQuery(id+"F16.imprint","IMPRINT",EDGE,{"derivedFrom":subQ0}),-1.0]])]});}
            var Q1;
            Q1=makeQuery(id+"F16.imprint","IMPRINT",FACE,{"disambiguationData":[TD([[makeQuery(id+"F16.imprint","IMPRINT",EDGE,{"derivedFrom":sQuery(id+"F16.wireOp",EDGE,"E80")}),-1.0]])]});
            var Q2;
            Q2=makeQuery(id+"F16.imprint","IMPRINT",FACE,{"disambiguationData":[TD([[makeQuery(id+"F16.imprint","IMPRINT",EDGE,{"derivedFrom":makeQuery(id+"F1.opExtrude","CAP_EDGE",EDGE,{"disambiguationData":[OSD([sQuery(id+"F0.wireOp",EDGE,"E1.left")])],"isStart":true})}),-1.0]])]});
            extrude(context, id + "F17", {"entities" : qUnion([Q0, Q1, Q2]), "depth" : 3 * mm});
        }
    });
